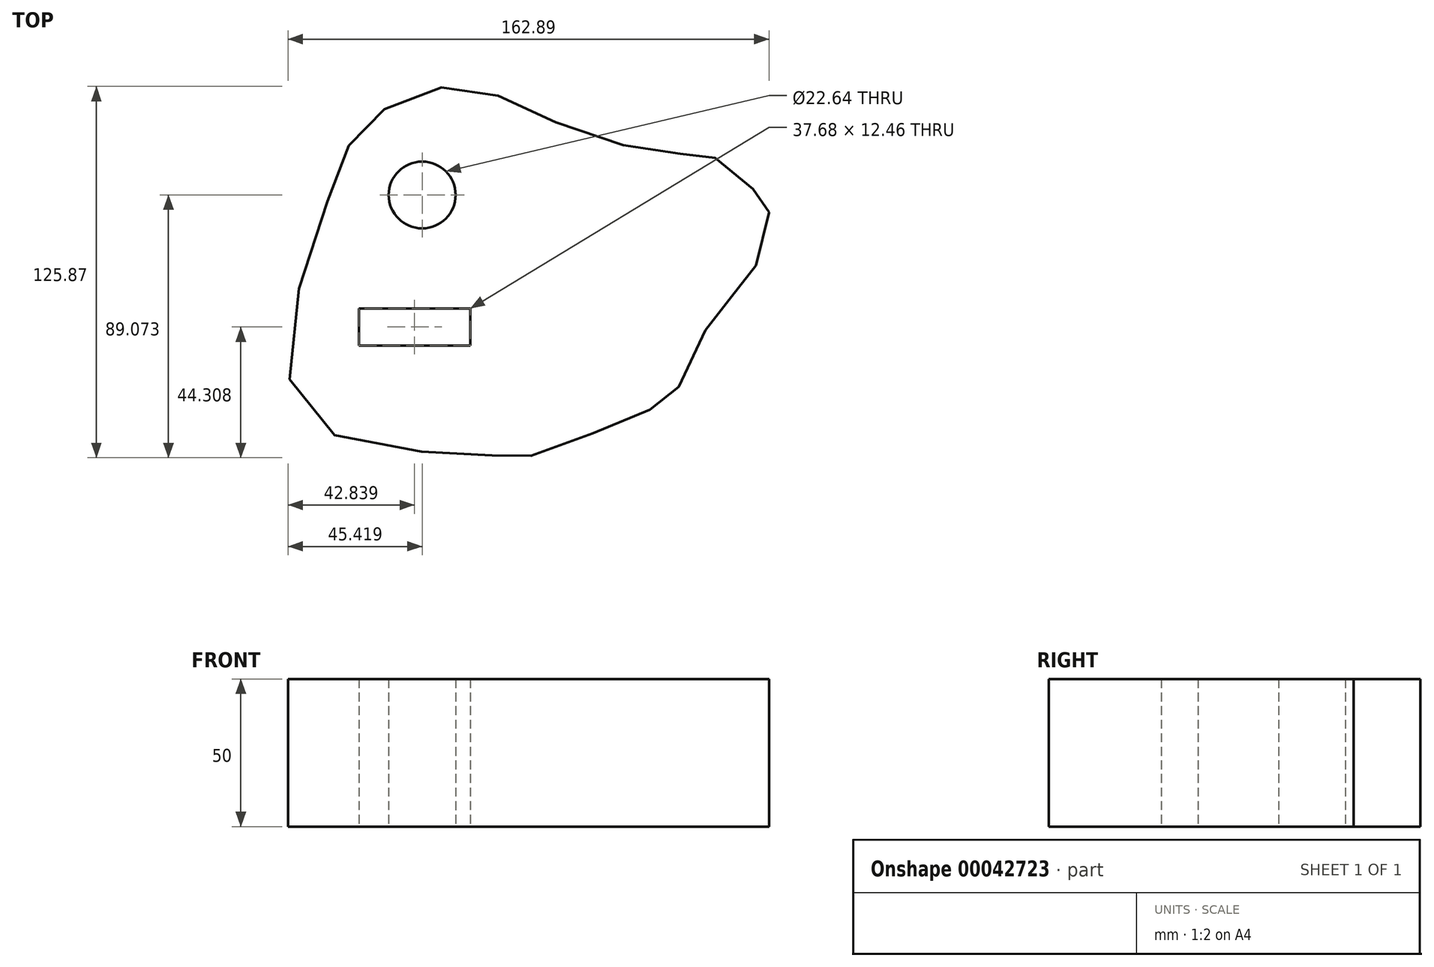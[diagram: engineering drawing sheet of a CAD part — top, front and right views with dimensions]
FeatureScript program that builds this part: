
annotation { "Feature Type Name" : "Feature", "Feature Type Description" : "" }
export const myFeature = defineFeature(function(context is Context, id is Id, definition is map)
    precondition{}
    {
        {
            var Q0;
            Q0=qCreatedBy(makeId("Top.planeOp"),FACE);
            var sketch = newSketch(context, id + "F0", { "sketchPlane" : qUnion([Q0])});
            skFitSpline(sketch, "E0", {"points": [v(-118.28, 29.45) * mm, v(-105.18, 56.02) * mm, v(-74.07, 68.38) * mm, v(-40.28, 55.87) * mm, v(0, 45.56) * mm, v(12.36, 44.43) * mm, v(28.54, 30.98) * mm, v(31.22, 25.8) * mm, v(22.69, 0) * mm, v(15.09, -5.22) * mm, v(0, -34.48) * mm, v(-11.4, -42.06) * mm, v(-49.93, -56.91) * mm, v(-66.42, -56.34) * mm, v(-126.7, -42) * mm, v(-118.28, 29.45) * mm]});
            skLineSegment(sketch, "E1.bottom", {"start": v(-107.67, -6.95) * mm, "end": v(-69.99, -6.95) * mm});
            skLineSegment(sketch, "E1.top", {"start": v(-107.67, -19.41) * mm, "end": v(-69.99, -19.41) * mm});
            skLineSegment(sketch, "E1.left", {"start": v(-107.67, -6.95) * mm, "end": v(-107.67, -19.41) * mm});
            skLineSegment(sketch, "E1.right", {"start": v(-69.99, -6.95) * mm, "end": v(-69.99, -19.41) * mm});
            skCircle(sketch, "E2", {"center": v(-86.25, 31.58) * mm, "radius": 11.32 * mm});
            skSolve(sketch);
        }
        {
            var Q0;
            Q0 = qSketchRegion(id + "F0", true);
            extrude(context, id + "F1", {"entities" : qUnion([Q0]), "depth" : 50 * mm});
        }
    });
